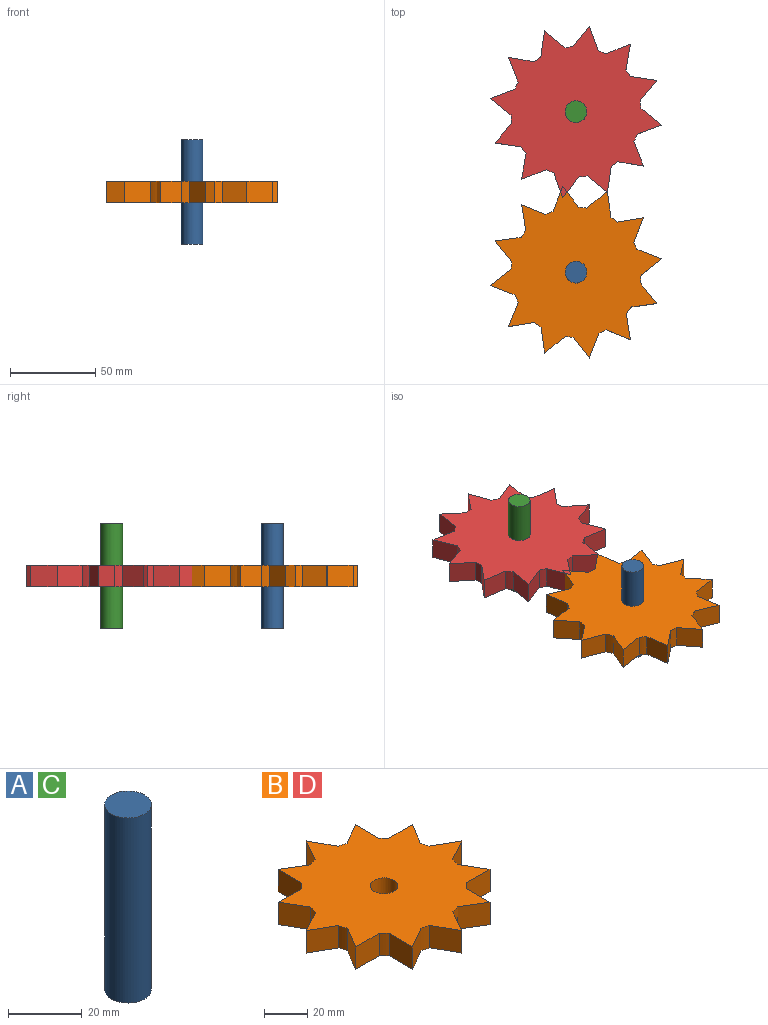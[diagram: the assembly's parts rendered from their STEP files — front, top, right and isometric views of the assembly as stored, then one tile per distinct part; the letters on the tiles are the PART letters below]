
ASSEMBLY  parts=4 mates=3
PART A: 3 faces, bbox 12.7x12.7x61.5 mm
  f0: cylinder r=6.35mm len=61.47mm, axis (0,0,-1), area 2452.5mm2, adj f1,f2
  f1: plane 12.7x12.7mm, normal (0,0,1), area 126.7mm2, adj f0
  f2: plane 12.7x12.7mm, normal (0,0,-1), area 126.7mm2, adj f0
PART B: 39 faces, bbox 101.6x101.6x12.7 mm
  f0: cylinder r=38.1mm len=12.7mm, axis (0,0,-1), area 59.4mm2, adj f12,f13,f35,f36
  f1: cylinder r=38.1mm len=12.7mm, axis (0,0,-1), area 59.4mm2, adj f12,f13,f33,f34
  f2: cylinder r=38.1mm len=12.7mm, axis (0,0,-1), area 59.4mm2, adj f12,f13,f31,f32
  f3: cylinder r=38.1mm len=12.7mm, axis (0,0,-1), area 59.4mm2, adj f12,f13,f29,f30
  f4: cylinder r=38.1mm len=12.7mm, axis (0,0,-1), area 59.4mm2, adj f12,f13,f27,f28
  f5: cylinder r=38.1mm len=12.7mm, axis (0,0,-1), area 59.4mm2, adj f12,f13,f25,f26
  f6: cylinder r=38.1mm len=12.7mm, axis (0,0,-1), area 59.4mm2, adj f12,f13,f23,f24
  f7: cylinder r=38.1mm len=12.7mm, axis (0,0,-1), area 59.4mm2, adj f12,f13,f21,f22
  f8: cylinder r=38.1mm len=12.7mm, axis (0,0,-1), area 59.4mm2, adj f12,f13,f19,f20
  f9: cylinder r=38.1mm len=12.7mm, axis (0,0,-1), area 59.4mm2, adj f12,f13,f17,f18
  f10: cylinder r=38.1mm len=12.7mm, axis (0,0,-1), area 59.4mm2, adj f12,f13,f15,f16
  f11: cylinder r=38.1mm len=12.7mm, axis (0,0,-1), area 59.4mm2, adj f12,f13,f14,f37
  f12: plane 101.6x101.6mm, normal (0,0,1), area 5566.3mm2, adj f0,f1,f2,f3,f4,f5,f6,f7
  f13: plane 101.6x101.6mm, normal (0,0,-1), area 5566.3mm2, adj f0,f1,f2,f3,f4,f5,f6,f7
  f14: plane 13.43x12.7mm, normal (0.87,0.48,0), area 195.1mm2, adj f11,f12,f13,f15
  f15: plane 13.49x12.7mm, normal (-0.87,0.5,0), area 197.4mm2, adj f10,f12,f13,f14
  f16: plane 13.17x12.7mm, normal (0.52,0.86,0), area 195.1mm2, adj f10,f12,f13,f17
  f17: plane 15.55x12.7mm, normal (-1,0,0), area 197.4mm2, adj f9,f12,f13,f16
  f18: plane 15.36x12.7mm, normal (0.02,1,0), area 195.1mm2, adj f9,f12,f13,f19
  f19: plane 13.43x12.7mm, normal (-0.86,-0.5,0), area 197.4mm2, adj f8,f12,f13,f18
  f20: plane 13.43x12.7mm, normal (-0.48,0.87,0), area 195.1mm2, adj f8,f12,f13,f21
  f21: plane 13.49x12.7mm, normal (-0.5,-0.87,0), area 197.4mm2, adj f7,f12,f13,f20
  f22: plane 13.17x12.7mm, normal (-0.86,0.52,0), area 195.1mm2, adj f7,f12,f13,f23
  f23: plane 15.55x12.7mm, normal (0,-1,0), area 197.4mm2, adj f6,f12,f13,f22
  f24: plane 15.36x12.7mm, normal (-1,0.02,0), area 195.1mm2, adj f6,f12,f13,f25
  f25: plane 13.43x12.7mm, normal (0.5,-0.86,0), area 197.4mm2, adj f5,f12,f13,f24
  f26: plane 13.43x12.7mm, normal (-0.87,-0.48,0), area 195.1mm2, adj f5,f12,f13,f27
  f27: plane 13.49x12.7mm, normal (0.87,-0.5,0), area 197.4mm2, adj f4,f12,f13,f26
  f28: plane 13.17x12.7mm, normal (-0.52,-0.86,0), area 195.1mm2, adj f4,f12,f13,f29
  f29: plane 15.55x12.7mm, normal (1,0,0), area 197.4mm2, adj f3,f12,f13,f28
  f30: plane 15.36x12.7mm, normal (-0.02,-1,0), area 195.1mm2, adj f3,f12,f13,f31
  f31: plane 13.43x12.7mm, normal (0.86,0.5,0), area 197.4mm2, adj f2,f12,f13,f30
  f32: plane 13.43x12.7mm, normal (0.48,-0.87,0), area 195.1mm2, adj f2,f12,f13,f33
  f33: plane 13.49x12.7mm, normal (0.5,0.87,0), area 197.4mm2, adj f1,f12,f13,f32
  f34: plane 13.17x12.7mm, normal (0.86,-0.52,0), area 195.1mm2, adj f1,f12,f13,f35
  f35: plane 15.55x12.7mm, normal (0,1,0), area 197.4mm2, adj f0,f12,f13,f34
  f36: plane 15.36x12.7mm, normal (1,-0.02,0), area 195.1mm2, adj f0,f12,f13,f37
  f37: plane 13.43x12.7mm, normal (-0.5,0.86,0), area 197.4mm2, adj f11,f12,f13,f36
  f38: cylinder r=6.35mm len=12.7mm, axis (0,0,1), area 506.7mm2, adj f12,f13
PART C: same geometry as A
PART D: same geometry as B
PLACE A t=(-23.43,-103.21,-0.93)mm
PLACE B rot(axis=(0,0,1),98.8deg) t=(-23.43,-103.21,0.09)mm
PLACE C t=(-23.43,-9.23,-0.93)mm fixed
PLACE D rot(axis=(0,0,-1),98.8deg) t=(-23.43,-9.23,0.09)mm
MATE revolute A.f0 <-> B.f38  axis (0,0,-1) through (-23.43,-103.21,6.44)mm
MATE revolute D.f38 <-> C.f0  axis (0,0,1) through (-23.43,-9.23,6.44)mm
MATE fastened C.f0 <-> A.f1  axis (0,0,1) through (-23.43,-9.23,37.17)mm
